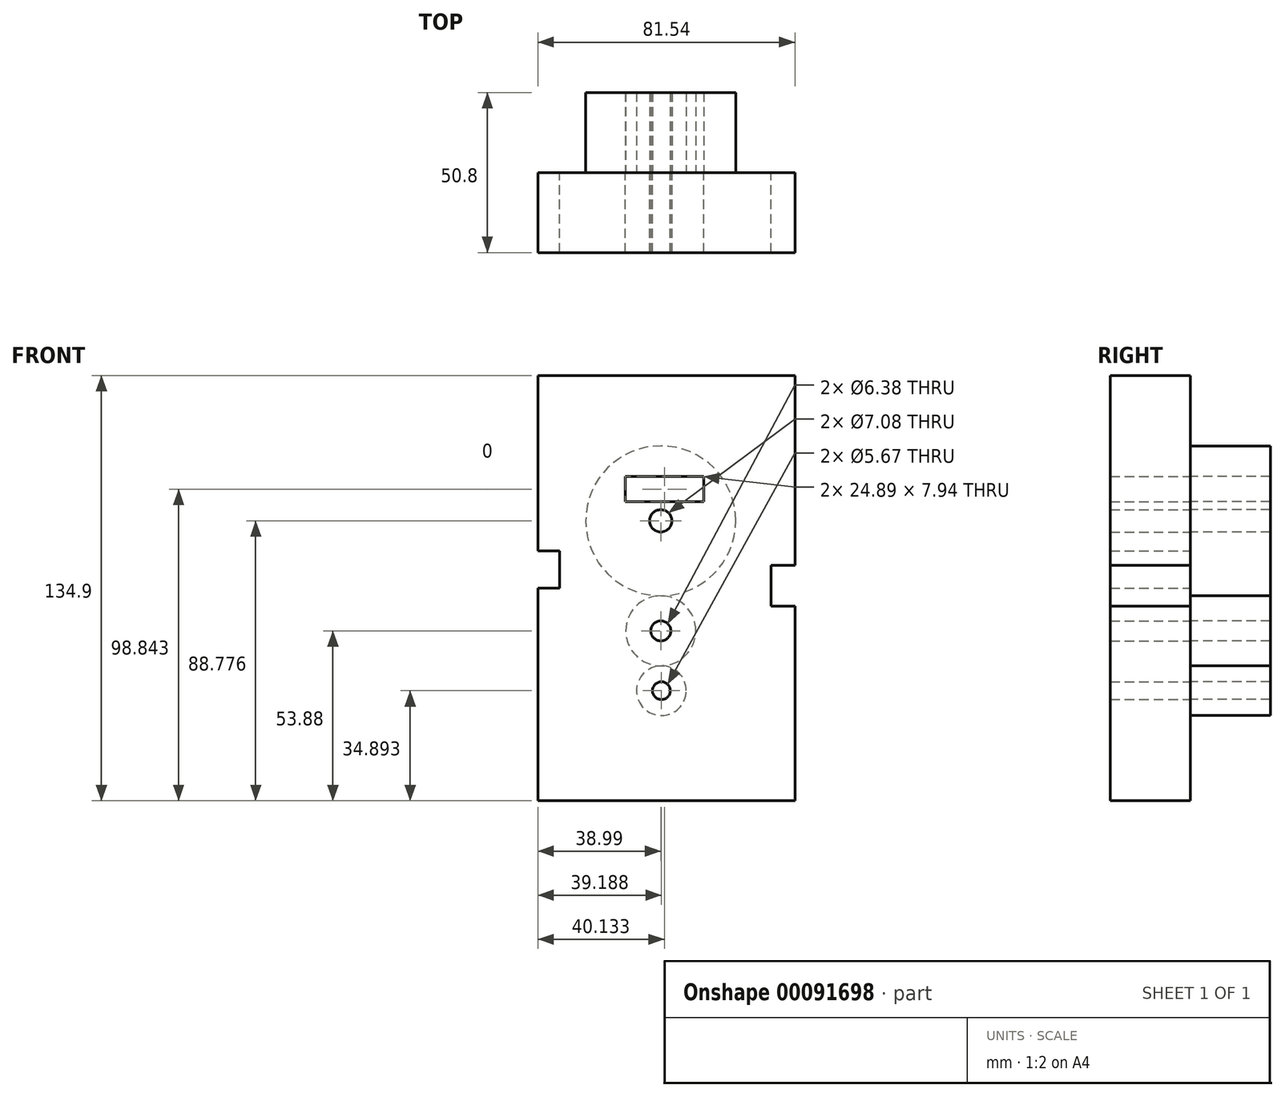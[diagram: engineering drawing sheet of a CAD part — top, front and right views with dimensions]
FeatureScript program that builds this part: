
annotation { "Feature Type Name" : "Feature", "Feature Type Description" : "" }
export const myFeature = defineFeature(function(context is Context, id is Id, definition is map)
    precondition{}
    {
        {
            var Q0;
            Q0=qCreatedBy(makeId("Front.planeOp"),FACE);
            var sketch = newSketch(context, id + "F0", { "sketchPlane" : qUnion([Q0])});
            skCircle(sketch, "E0", {"center": v(0, 34.9) * mm, "radius": 23.78 * mm});
            skCircle(sketch, "E1", {"center": v(0, 0) * mm, "radius": 11.11 * mm});
            skCircle(sketch, "E2", {"center": v(0.2, -18.99) * mm, "radius": 7.88 * mm});
            skCircle(sketch, "E3", {"center": v(0, 34.9) * mm, "radius": 3.54 * mm});
            skCircle(sketch, "E4", {"center": v(0, 0) * mm, "radius": 3.19 * mm});
            skCircle(sketch, "E5", {"center": v(0.2, -18.99) * mm, "radius": 2.83 * mm});
            skLineSegment(sketch, "E6.bottom", {"start": v(-39, 81.02) * mm, "end": v(42.55, 81.02) * mm});
            skLineSegment(sketch, "E6.top", {"start": v(-39, -53.88) * mm, "end": v(42.55, -53.88) * mm});
            skLineSegment(sketch, "E6.left", {"start": v(-39, 81.02) * mm, "end": v(-39, 25.38) * mm});
            skLineSegment(sketch, "E6.right", {"start": v(42.55, 81.02) * mm, "end": v(42.55, 20.8) * mm});
            skPoint(sketch, "E7.oppositeSnap0", {"position": v(-39, 13.57) * mm});
            skLineSegment(sketch, "E7.bottom", {"start": v(-39, 25.38) * mm, "end": v(-32.13, 25.38) * mm});
            skLineSegment(sketch, "E7.top", {"start": v(-39, 13.57) * mm, "end": v(-32.13, 13.57) * mm});
            skLineSegment(sketch, "E7.right", {"start": v(-32.13, 25.38) * mm, "end": v(-32.13, 13.57) * mm});
            skLineSegment(sketch, "E8.bottom", {"start": v(42.55, 20.8) * mm, "end": v(34.93, 20.8) * mm});
            skLineSegment(sketch, "E8.top", {"start": v(42.55, 7.85) * mm, "end": v(34.93, 7.85) * mm});
            skLineSegment(sketch, "E8.right", {"start": v(34.93, 20.8) * mm, "end": v(34.93, 7.85) * mm});
            skLineSegment(sketch, "E9.trimOffspring", {"start": v(42.55, 7.85) * mm, "end": v(42.55, -53.88) * mm});
            skLineSegment(sketch, "E10.trimOffspring", {"start": v(-39, 13.57) * mm, "end": v(-39, -53.88) * mm});
            skLineSegment(sketch, "E11.bottom", {"start": v(13.59, 48.94) * mm, "end": v(-11.3, 48.94) * mm});
            skLineSegment(sketch, "E11.top", {"start": v(13.59, 41) * mm, "end": v(-11.3, 41) * mm});
            skLineSegment(sketch, "E11.left", {"start": v(13.59, 48.94) * mm, "end": v(13.59, 41) * mm});
            skLineSegment(sketch, "E11.right", {"start": v(-11.3, 48.94) * mm, "end": v(-11.3, 41) * mm});
            skSolve(sketch);
        }
        {
            var Q0;
            Q0=makeQuery(id+"F0.imprint","IMPRINT",FACE,{"disambiguationData":[TD([[makeQuery(id+"F0.imprint","IMPRINT",EDGE,{"derivedFrom":sQuery(id+"F0.wireOp",EDGE,"E0")}),1.0]])]});
            var Q1;
            Q1=makeQuery(id+"F0.imprint","IMPRINT",FACE,{"disambiguationData":[TD([[makeQuery(id+"F0.imprint","IMPRINT",EDGE,{"derivedFrom":sQuery(id+"F0.wireOp",EDGE,"E4")}),-1.0]])]});
            var Q2;
            Q2=makeQuery(id+"F0.imprint","IMPRINT",FACE,{"disambiguationData":[TD([[makeQuery(id+"F0.imprint","IMPRINT",EDGE,{"derivedFrom":sQuery(id+"F0.wireOp",EDGE,"E2")}),1.0]])]});
            extrude(context, id + "F1", {"entities" : qUnion([Q0, Q1, Q2]), "oppositeDirection" : true, "depth" : 25.4 * mm});
        }
        {
            var Q0;
            {var subQ1=sQuery(id+"F0.wireOp",EDGE,"E0");Q0=makeQuery(id+"F0.imprint","IMPRINT",FACE,{"disambiguationData":[TD([[makeQuery(id+"F0.imprint","IMPRINT",EDGE,{"derivedFrom":subQ1}),-1.0]])]});}
            var Q1;
            Q1=makeQuery(id+"F0.imprint","IMPRINT",FACE,{"disambiguationData":[TD([[makeQuery(id+"F0.imprint","IMPRINT",EDGE,{"derivedFrom":sQuery(id+"F0.wireOp",EDGE,"E2")}),1.0]])]});
            var Q2;
            Q2=makeQuery(id+"F0.imprint","IMPRINT",FACE,{"disambiguationData":[TD([[makeQuery(id+"F0.imprint","IMPRINT",EDGE,{"derivedFrom":sQuery(id+"F0.wireOp",EDGE,"E4")}),-1.0]])]});
            var Q3;
            Q3=makeQuery(id+"F0.imprint","IMPRINT",FACE,{"disambiguationData":[TD([[makeQuery(id+"F0.imprint","IMPRINT",EDGE,{"derivedFrom":sQuery(id+"F0.wireOp",EDGE,"E0")}),1.0]])]});
            extrude(context, id + "F2", {"entities" : qUnion([Q0, Q1, Q2, Q3]), "depth" : 25.4 * mm});
        }
    });
